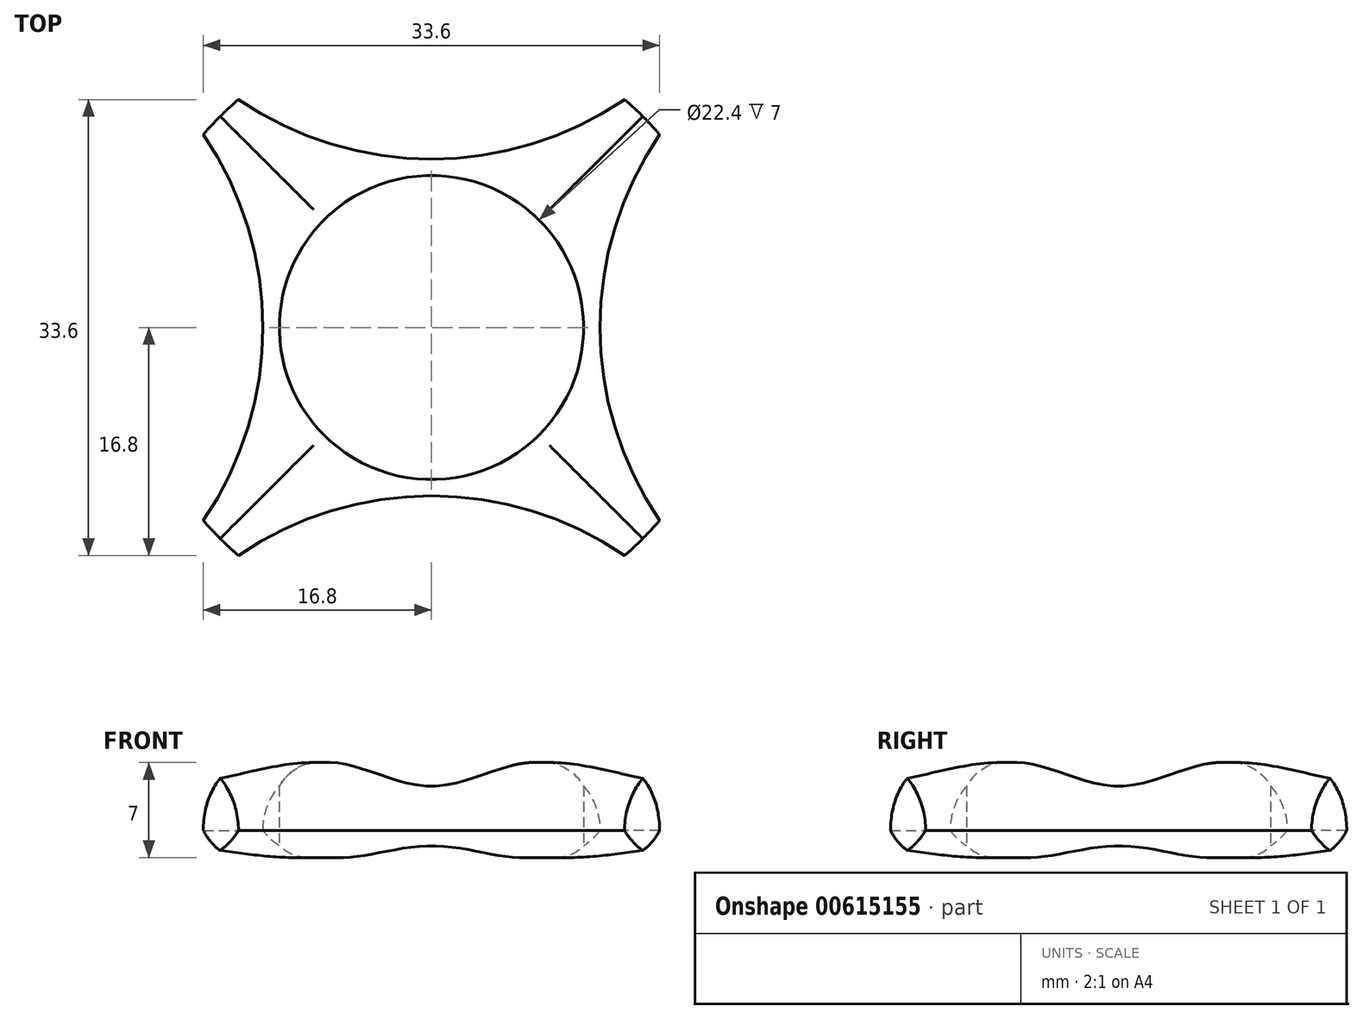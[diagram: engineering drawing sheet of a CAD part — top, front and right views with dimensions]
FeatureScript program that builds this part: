
annotation { "Feature Type Name" : "Feature", "Feature Type Description" : "" }
export const myFeature = defineFeature(function(context is Context, id is Id, definition is map)
    precondition{}
    {
        {
            var Q0;
            Q0=qCreatedBy(makeId("Top.planeOp"),FACE);
            var sketch = newSketch(context, id + "F0", { "sketchPlane" : qUnion([Q0])});
            skCircle(sketch, "E0", {"center": v(0, 0) * mm, "radius": 11.2 * mm});
            skArc(sketch, "E1", {"start": v(-16.8, -14.2) * mm, "mid": v(-15.56, -15.56) * mm, "end": v(-14.2, -16.8) * mm});
            skArc(sketch, "E2", {"start": v(-16.8, -14.2) * mm, "mid": v(-12.4, 0) * mm, "end": v(-16.8, 14.2) * mm});
            skArc(sketch, "E3.1.0", {"start": v(14.2, -16.8) * mm, "mid": v(0, -12.4) * mm, "end": v(-14.2, -16.8) * mm});
            skArc(sketch, "E3.2.0", {"start": v(16.8, 14.2) * mm, "mid": v(12.4, 0) * mm, "end": v(16.8, -14.2) * mm});
            skArc(sketch, "E3.3.0", {"start": v(-14.2, 16.8) * mm, "mid": v(0, 12.4) * mm, "end": v(14.2, 16.8) * mm});
            skArc(sketch, "E4.trimOffspring", {"start": v(-14.2, 16.8) * mm, "mid": v(-15.56, 15.56) * mm, "end": v(-16.8, 14.2) * mm});
            skArc(sketch, "E5.trimOffspring", {"start": v(16.8, 14.2) * mm, "mid": v(15.56, 15.56) * mm, "end": v(14.2, 16.8) * mm});
            skArc(sketch, "E6.trimOffspring", {"start": v(14.2, -16.8) * mm, "mid": v(15.56, -15.56) * mm, "end": v(16.8, -14.2) * mm});
            skSolve(sketch);
        }
        {
            var Q0;
            Q0 = qSketchRegion(id + "F0", true);
            extrude(context, id + "F1", {"entities" : qUnion([Q0]), "depth" : 7 * mm, "offsetDistance" : 25 * mm});
        }
        {
            var Q0;
            Q0=makeQuery(id+"F1.opExtrude","CAP_EDGE",EDGE,{"disambiguationData":[OSD([sQuery(id+"F0.wireOp",EDGE,"E3.2.0")])],"isStart":false});
            var Q1;
            Q1=makeQuery(id+"F1.opExtrude","CAP_EDGE",EDGE,{"disambiguationData":[OSD([sQuery(id+"F0.wireOp",EDGE,"E2")])],"isStart":false});
            var Q2;
            Q2=makeQuery(id+"F1.opExtrude","CAP_EDGE",EDGE,{"disambiguationData":[OSD([sQuery(id+"F0.wireOp",EDGE,"E3.3.0")])],"isStart":false});
            var Q3;
            Q3=makeQuery(id+"F1.opExtrude","CAP_EDGE",EDGE,{"disambiguationData":[OSD([sQuery(id+"F0.wireOp",EDGE,"E4.trimOffspring")])],"isStart":false});
            var Q4;
            Q4=makeQuery(id+"F1.opExtrude","CAP_EDGE",EDGE,{"disambiguationData":[OSD([sQuery(id+"F0.wireOp",EDGE,"E1")])],"isStart":false});
            var Q5;
            Q5=makeQuery(id+"F1.opExtrude","CAP_EDGE",EDGE,{"disambiguationData":[OSD([sQuery(id+"F0.wireOp",EDGE,"E3.1.0")])],"isStart":false});
            var Q6;
            Q6=makeQuery(id+"F1.opExtrude","CAP_EDGE",EDGE,{"disambiguationData":[OSD([sQuery(id+"F0.wireOp",EDGE,"E5.trimOffspring")])],"isStart":false});
            var Q7;
            Q7=makeQuery(id+"F1.opExtrude","CAP_EDGE",EDGE,{"disambiguationData":[OSD([sQuery(id+"F0.wireOp",EDGE,"E6.trimOffspring")])],"isStart":false});
            fillet(context, id + "F2", {"entities" : qUnion([Q0, Q1, Q2, Q3, Q4, Q5, Q6, Q7]), "radius" : 5 * mm, "tangentPropagation" : true, "allowEdgeOverflow" : false});
        }
        {
            var Q0;
            Q0=makeQuery(id+"F1.opExtrude","CAP_EDGE",EDGE,{"disambiguationData":[OSD([sQuery(id+"F0.wireOp",EDGE,"E3.2.0")])],"isStart":true});
            var Q1;
            Q1=makeQuery(id+"F1.opExtrude","CAP_EDGE",EDGE,{"disambiguationData":[OSD([sQuery(id+"F0.wireOp",EDGE,"E3.3.0")])],"isStart":true});
            var Q2;
            Q2=makeQuery(id+"F1.opExtrude","CAP_EDGE",EDGE,{"disambiguationData":[OSD([sQuery(id+"F0.wireOp",EDGE,"E2")])],"isStart":true});
            var Q3;
            Q3=makeQuery(id+"F1.opExtrude","CAP_EDGE",EDGE,{"disambiguationData":[OSD([sQuery(id+"F0.wireOp",EDGE,"E3.1.0")])],"isStart":true});
            fillet(context, id + "F3", {"entities" : qUnion([Q0, Q1, Q2, Q3]), "radius" : 5 * mm, "tangentPropagation" : true, "allowEdgeOverflow" : false});
        }
    });
